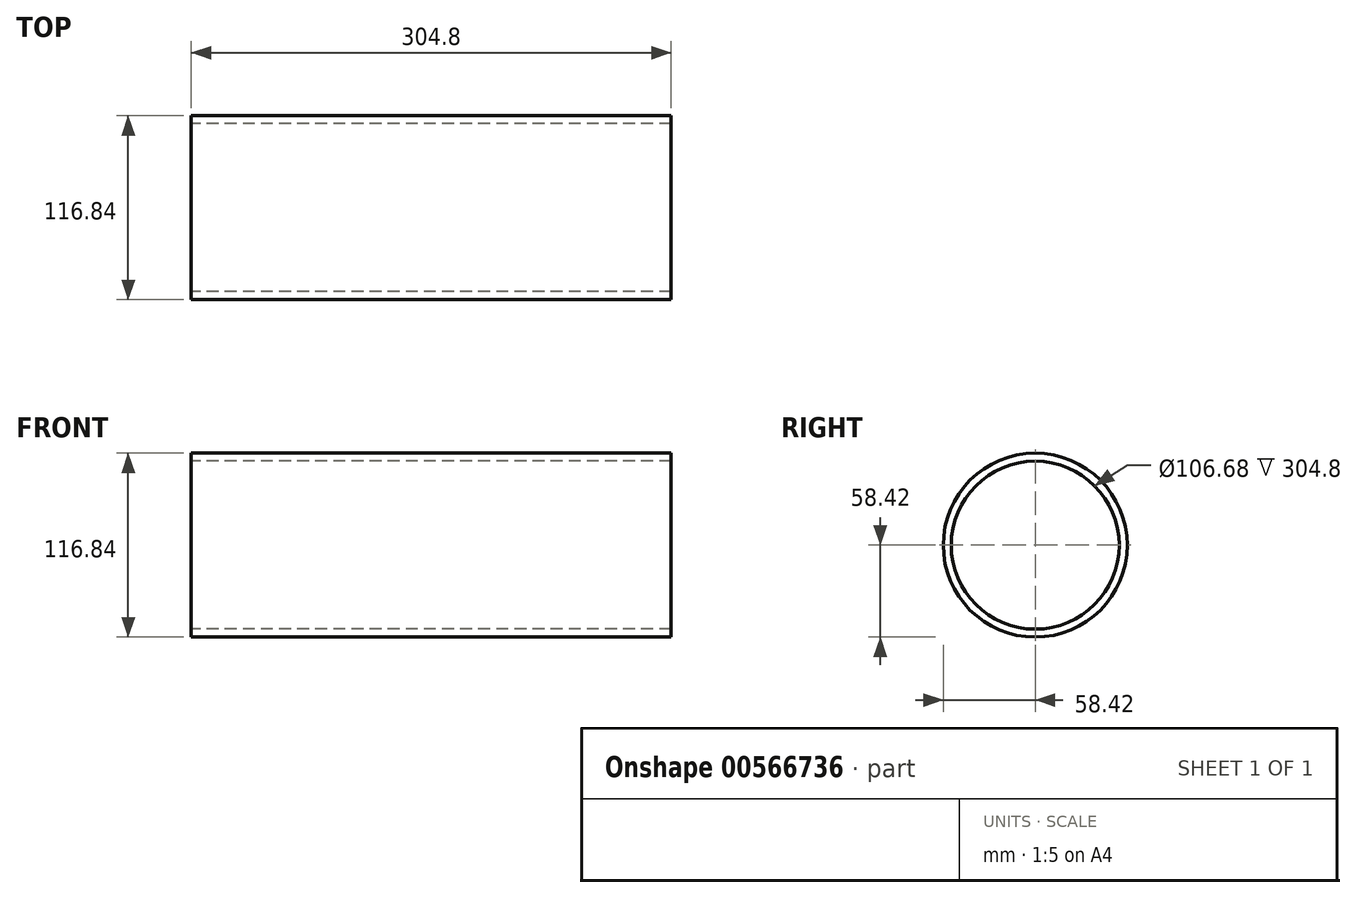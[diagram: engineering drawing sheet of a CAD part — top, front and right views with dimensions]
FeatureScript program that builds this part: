
annotation { "Feature Type Name" : "Feature", "Feature Type Description" : "" }
export const myFeature = defineFeature(function(context is Context, id is Id, definition is map)
    precondition{}
    {
        {
            var Q0;
            Q0=qCreatedBy(makeId("Right.planeOp"),FACE);
            var sketch = newSketch(context, id + "F0", { "sketchPlane" : qUnion([Q0])});
            skCircle(sketch, "E0", {"center": v(0, 0) * mm, "radius": 58.42 * mm});
            skCircle(sketch, "E1", {"center": v(0, 0) * mm, "radius": 53.34 * mm});
            skSolve(sketch);
        }
        {
            var Q0;
            Q0=makeQuery(id+"F0.imprint","IMPRINT",FACE,{"disambiguationData":[TD([[makeQuery(id+"F0.imprint","IMPRINT",EDGE,{"derivedFrom":sQuery(id+"F0.wireOp",EDGE,"E0")}),1.0]])]});
            extrude(context, id + "F1", {"entities" : qUnion([Q0]), "endBound" : BoundingType.SYMMETRIC, "depth" : 304.8 * mm, "offsetDistance" : 25.4 * mm});
        }
    });
